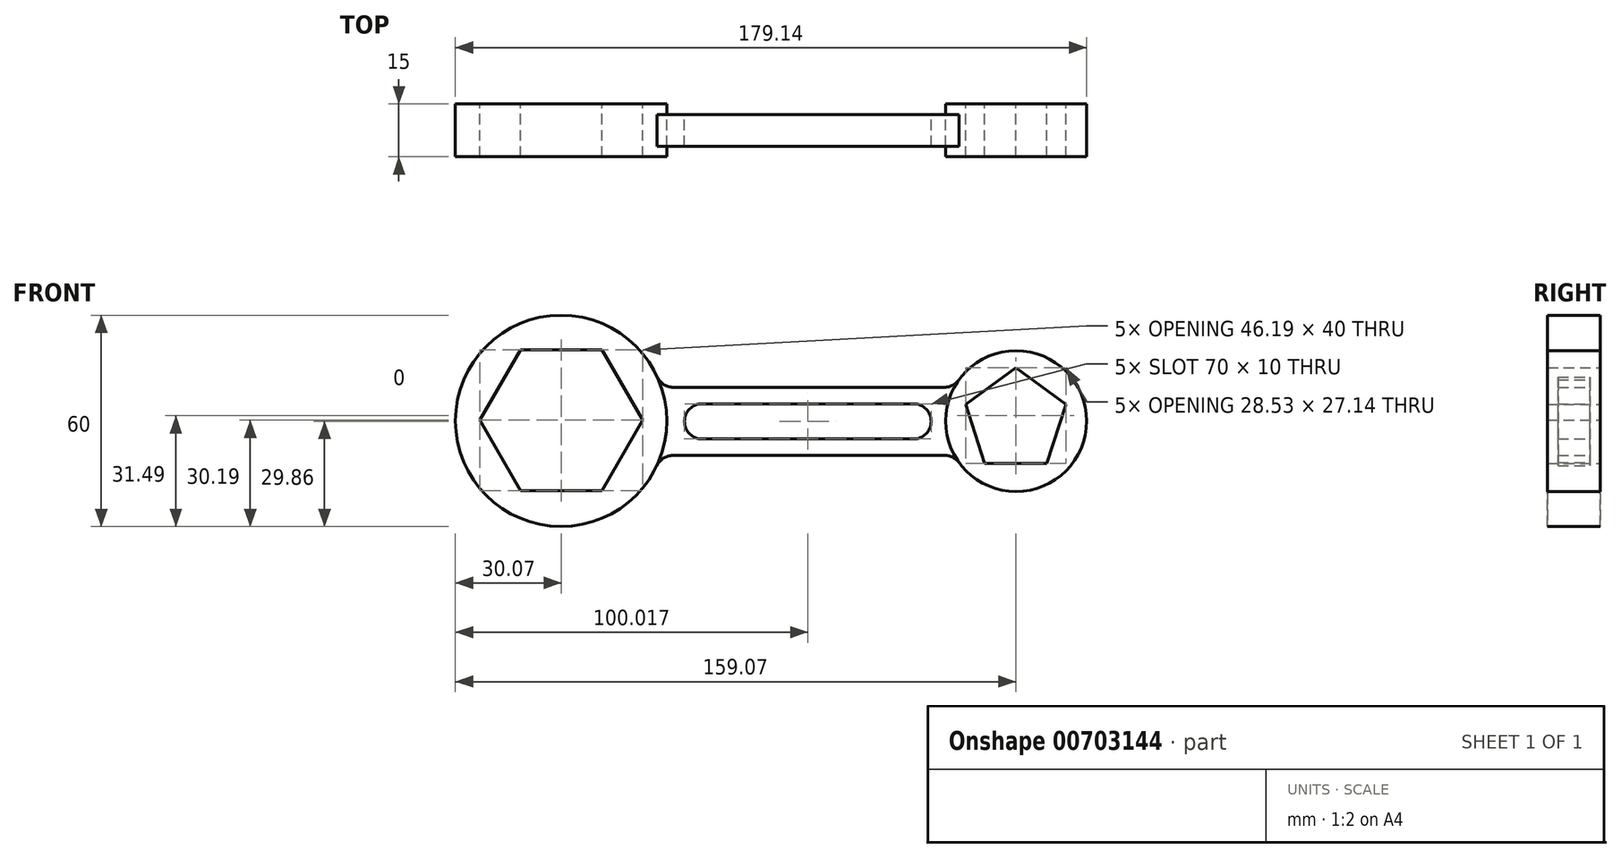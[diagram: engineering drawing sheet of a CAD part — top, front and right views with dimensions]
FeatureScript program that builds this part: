
annotation { "Feature Type Name" : "Feature", "Feature Type Description" : "" }
export const myFeature = defineFeature(function(context is Context, id is Id, definition is map)
    precondition{}
    {
        {
            var Q0;
            Q0=qCreatedBy(makeId("Front.planeOp"),FACE);
            var sketch = newSketch(context, id + "F0", { "sketchPlane" : qUnion([Q0])});
            skLineSegment(sketch, "E0.0", {"start": v(-23.1, 0) * mm, "end": v(-11.55, 20) * mm});
            skLineSegment(sketch, "E0.1", {"start": v(-11.55, 20) * mm, "end": v(11.55, 20) * mm});
            skLineSegment(sketch, "E0.2", {"start": v(11.55, 20) * mm, "end": v(23.1, 0) * mm});
            skLineSegment(sketch, "E0.3", {"start": v(23.1, 0) * mm, "end": v(11.55, -20) * mm});
            skLineSegment(sketch, "E0.4", {"start": v(11.55, -20) * mm, "end": v(-11.55, -20) * mm});
            skLineSegment(sketch, "E0.5", {"start": v(-11.55, -20) * mm, "end": v(-23.1, 0) * mm});
            skLineSegment(sketch, "E1", {"start": v(31.77, 9.35) * mm, "end": v(108.77, 9.35) * mm});
            skLineSegment(sketch, "E2", {"start": v(31.64, -10) * mm, "end": v(108.89, -10) * mm});
            skLineSegment(sketch, "E3.bottom", {"start": v(39.95, 4.67) * mm, "end": v(99.95, 4.67) * mm});
            skLineSegment(sketch, "E3.top", {"start": v(39.95, -5.33) * mm, "end": v(99.95, -5.33) * mm});
            skLineSegment(sketch, "E3.left", {"start": v(34.95, -0.33) * mm, "end": v(34.95, -0.33) * mm});
            skLineSegment(sketch, "E3.right", {"start": v(104.95, -0.33) * mm, "end": v(104.95, -0.33) * mm});
            skLineSegment(sketch, "E4.0", {"start": v(129, 14.87) * mm, "end": v(143.27, 4.5) * mm});
            skLineSegment(sketch, "E4.1", {"start": v(143.27, 4.5) * mm, "end": v(137.82, -12.27) * mm});
            skLineSegment(sketch, "E4.2", {"start": v(137.82, -12.27) * mm, "end": v(120.18, -12.27) * mm});
            skLineSegment(sketch, "E4.3", {"start": v(120.18, -12.27) * mm, "end": v(114.73, 4.5) * mm});
            skLineSegment(sketch, "E4.4", {"start": v(114.73, 4.5) * mm, "end": v(129, 14.87) * mm});
            skArc(sketch, "E5.filletArc", {"start": v(104.95, -0.33) * mm, "mid": v(103.48, 3.2) * mm, "end": v(99.95, 4.67) * mm});
            skArc(sketch, "E6.filletArc", {"start": v(99.95, -5.33) * mm, "mid": v(103.48, -3.87) * mm, "end": v(104.95, -0.33) * mm});
            skArc(sketch, "E7.filletArc", {"start": v(39.95, 4.67) * mm, "mid": v(36.41, 3.2) * mm, "end": v(34.95, -0.33) * mm});
            skArc(sketch, "E8.filletArc", {"start": v(34.95, -0.33) * mm, "mid": v(36.41, -3.87) * mm, "end": v(39.95, -5.33) * mm});
            skArc(sketch, "E9", {"start": v(112.92, -12.06) * mm, "mid": v(149.06, -0.17) * mm, "end": v(112.83, 11.43) * mm});
            skArc(sketch, "E10.filletArc", {"start": v(108.77, 9.35) * mm, "mid": v(111.05, 9.9) * mm, "end": v(112.83, 11.43) * mm});
            skArc(sketch, "E11.filletArc", {"start": v(112.92, -12.06) * mm, "mid": v(111.15, -10.55) * mm, "end": v(108.89, -10) * mm});
            skArc(sketch, "E12", {"start": v(27.22, 12.27) * mm, "mid": v(-30.07, -0.05) * mm, "end": v(27.11, -12.9) * mm});
            skArc(sketch, "E13.filletArc", {"start": v(27.22, 12.27) * mm, "mid": v(29.07, 10.14) * mm, "end": v(31.77, 9.35) * mm});
            skArc(sketch, "E14.filletArc", {"start": v(31.64, -10) * mm, "mid": v(28.96, -10.8) * mm, "end": v(27.11, -12.9) * mm});
            skArc(sketch, "E15", {"start": v(27.11, -12.9) * mm, "mid": v(29.93, -0.32) * mm, "end": v(27.22, 12.27) * mm});
            skArc(sketch, "E16", {"start": v(112.83, 11.43) * mm, "mid": v(109.07, -0.33) * mm, "end": v(112.92, -12.06) * mm});
            skSolve(sketch);
        }
        {
            var Q0;
            Q0=makeQuery(id+"F0.imprint","IMPRINT",FACE,{"disambiguationData":[TD([[makeQuery(id+"F0.imprint","IMPRINT",EDGE,{"derivedFrom":sQuery(id+"F0.wireOp",EDGE,"E0.0")}),1.0]])]});
            var Q1;
            Q1=makeQuery(id+"F0.imprint","IMPRINT",FACE,{"disambiguationData":[TD([[makeQuery(id+"F0.imprint","IMPRINT",EDGE,{"derivedFrom":sQuery(id+"F0.wireOp",EDGE,"E4.0")}),1.0]])]});
            extrude(context, id + "F1", {"entities" : qUnion([Q0, Q1]), "depth" : 15 * mm, "offsetDistance" : 25 * mm});
        }
        {
            var Q0;
            Q0=makeQuery(id+"F0.imprint","IMPRINT",FACE,{"disambiguationData":[TD([[makeQuery(id+"F0.imprint","IMPRINT",EDGE,{"derivedFrom":sQuery(id+"F0.wireOp",EDGE,"E1")}),-1.0]])]});
            extrude(context, id + "F2", {"entities" : qUnion([Q0]), "depth" : 12 * mm, "offsetDistance" : 25 * mm});
        }
        {
            var Q0;
            Q0=makeQuery(id+"F0.imprint","IMPRINT",FACE,{"disambiguationData":[TD([[makeQuery(id+"F0.imprint","IMPRINT",EDGE,{"derivedFrom":sQuery(id+"F0.wireOp",EDGE,"E1")}),-1.0]])]});
            extrude(context, id + "F3", {"entities" : qUnion([Q0]), "operationType" : NewBodyOperationType.REMOVE, "depth" : 3 * mm, "offsetDistance" : 25 * mm});
        }
    });
